# Revit family: TESK_Насос вертикальный_SVM(T)-200
name_source: partatom
category: Оборудование
units: mm (PartAtom-declared; Revit-internal decimal feet)

## family parameters
Всегда вертикально = Да
Классификация = Насос
На основе рабочей плоскости = Нет
Общий = Нет
При загрузке вырезать с полостями = Нет
Размер круглого соединителя = Использовать диаметр
Тип детали = Вставляется
Точка расчета площади = Нет

## types (34) — shared parameters
ADSK_Версия Revit = 2019
ADSK_Версия семейства = 1.0
ADSK_Диаметр условный = 150 мм
ADSK_Единица измерения = шт.
ADSK_Завод-изготовитель = TESK
ADSK_Классификация нагрузок = Прочее
ADSK_Количество = 1
ADSK_Количество фаз = 3
ADSK_Количество фаз числовое = 3
ADSK_Коэффициент мощности = 1
ADSK_Наименование краткое = Вертикальный многоступенчатый центробежный насос
ADSK_Напряжение = 400 В
URL = www.teskpump.ru
Материал_1 = TESK_Черный_Условный
Материал_2 = TESK_Нержавеющая сталь
Материал_КорпусДвигателя = TESK_Черный_Ребра_Условный
Таблица_Поиска = TESK_SVM(T)-200
УГО_Длина = 490 мм
Фланец_Толщина = 30 мм

## per-type parameters (varying)
| type | ADSK_Код изделия | ADSK_Масса | ADSK_Масса_Текст | ADSK_Наименование | ADSK_Номинальная мощность | ADSK_Полная мощность | D_Башня | Высота_Башня | Высота_Корпуса | Двигатель_Высота | Двигатель_ОтступКоробки | Двигатель_Ширина | Материал_КорпусУлитка | Напор максимальный | Толщина_ФланцаДвигателя |
| SVM 200-1-B 18.5kW 3x380V 50Hz IE3 | 77200-10-20003380NSSF | 311 | 311 | Вертикальный многоступенчатый центробежный насос SVM, DN150, PN25-40, Hmax=25.5м (3x380V 50Hz IE3) | 19 кВт | 19 кВ·А | 263 мм | 320 мм | 907 мм | 610 мм | 260 мм | 350 мм | TESK_Нержавеющая сталь | 25.5 | 18 мм |
| SVM 200-1-A 22kW 3x380V 50Hz IE3 | 77200-10-10003380NSSF | 347 | 347 | Вертикальный многоступенчатый центробежный насос SVM, DN150, PN25-40, Hmax=29м (3x380V 50Hz IE3) | 22 кВт | 22 кВ·А | 270 мм | 320 мм | 907 мм | 645 мм | 285 мм | 360 мм | TESK_Нержавеющая сталь | 29 | 19 мм |
| SVM 200-1 30kW 3x380V 50Hz IE3 | 77200-100003380NSSF | 403 | 403 | Вертикальный многоступенчатый центробежный насос SVM, DN150, PN25-40, Hmax=38.5м (3x380V 50Hz IE3) | 30 кВт | 30 кВ·А | 300 мм | 320 мм | 907 мм | 705 мм | 310 мм | 400 мм | TESK_Нержавеющая сталь | 38.5 | 21 мм |
| SVM 200-2-2B 37kW 3x380V 50Hz IE3 | 77200-20-220003380NSSF | 447 | 447 | Вертикальный многоступенчатый центробежный насос SVM, DN150, PN25-40, Hmax=53м (3x380V 50Hz IE3) | 37 кВт | 37 кВ·А | 300 мм | 360 мм | 1101 мм | 705 мм | 310 мм | 400 мм | TESK_Нержавеющая сталь | 53 | 21 мм |
| SVM 200-2-A 45kW 3x380V 50Hz IE3 | 77200-20-210003380NSSF | 504 | 504 | Вертикальный многоступенчатый центробежный насос SVM, DN150, PN25-40, Hmax=59.5м (3x380V 50Hz IE3) | 45 кВт | 45 кВ·А | 345 мм | 360 мм | 1101 мм | 740 мм | 340 мм | 460 мм | TESK_Нержавеющая сталь | 59.5 | 22 мм |
| SVM 200-2-A 55kW 3x380V 50Hz IE3 | 77200-20-10003380NSSF | 595 | 595 | Вертикальный многоступенчатый центробежный насос SVM, DN150, PN25-40, Hmax=69м (3x380V 50Hz IE3) | 55 кВт | 55 кВ·А | 413 мм | 380 мм | 1131 мм | 810 мм | 370 мм | 550 мм | TESK_Нержавеющая сталь | 69 | 24 мм |
| SVM 200-2 55kW 3x380V 50Hz IE3 | 77200-200003380NSSF | 595 | 595 | Вертикальный многоступенчатый центробежный насос SVM, DN150, PN25-40, Hmax=78.5м (3x380V 50Hz IE3) | 55 кВт | 55 кВ·А | 413 мм | 380 мм | 1131 мм | 810 мм | 370 мм | 550 мм | TESK_Нержавеющая сталь | 78.5 | 24 мм |
| SVM 200-3-2B 75kW 3x380V 50Hz IE3 | 77200-30-220003380NSSF | 748 | 748 | Вертикальный многоступенчатый центробежный насос SVM, DN150, PN25-40, Hmax=91.5м (3x380V 50Hz IE3) | 75 кВт | 75 кВ·А | 435 мм | 420 мм | 1325 мм | 870 мм | 410 мм | 580 мм | TESK_Нержавеющая сталь | 91.5 | 26 мм |
| SVM 200-3-A-B 75kW 3x380V 50Hz IE3 | 77200-30-1-20003380NSSF | 748 | 748 | Вертикальный многоступенчатый центробежный насос SVM, DN150, PN25-40, Hmax=95м (3x380V 50Hz IE3) | 75 кВт | 75 кВ·А | 435 мм | 420 мм | 1325 мм | 870 мм | 410 мм | 580 мм | TESK_Нержавеющая сталь | 95 | 26 мм |
| SVM 200-3-2A 75kW 3x380V 50Hz IE3 | 77200-30-210003380NSSF | 748 | 748 | Вертикальный многоступенчатый центробежный насос SVM, DN150, PN25-40, Hmax=99.5м (3x380V 50Hz IE3) | 75 кВт | 75 кВ·А | 435 мм | 420 мм | 1325 мм | 870 мм | 410 мм | 580 мм | TESK_Нержавеющая сталь | 99.5 | 26 мм |
| SVM 200-3-B 75kW 3x380V 50Hz IE3 | 77200-30-20003380NSSF | 748 | 748 | Вертикальный многоступенчатый центробежный насос SVM, DN150, PN25-40, Hmax=104.5м (3x380V 50Hz IE3) | 75 кВт | 75 кВ·А | 435 мм | 420 мм | 1325 мм | 870 мм | 410 мм | 580 мм | TESK_Нержавеющая сталь | 104.5 | 26 мм |
| SVM 200-3-A 75kW 3x380V 50Hz IE3 | 77200-30-10003380NSSF | 748 | 748 | Вертикальный многоступенчатый центробежный насос SVM, DN150, PN25-40, Hmax=108м (3x380V 50Hz IE3) | 75 кВт | 75 кВ·А | 435 мм | 420 мм | 1325 мм | 870 мм | 410 мм | 580 мм | TESK_Нержавеющая сталь | 108 | 26 мм |
| SVM 200-3 90kW 3x380V 50Hz IE3 | 77200-300003380NSSF | 816 | 816 | Вертикальный многоступенчатый центробежный насос SVM, DN150, PN25-40, Hmax=117.5м (3x380V 50Hz IE3) | 90 кВт | 90 кВ·А | 435 мм | 420 мм | 1325 мм | 920 мм | 410 мм | 580 мм | TESK_Нержавеющая сталь | 117.5 | 28 мм |
| SVM 200-4-2B 90kW 3x380V 50Hz IE3 | 77200-40-220003380NSSF | 830 | 830 | Вертикальный многоступенчатый центробежный насос SVM, DN150, PN25-40, Hmax=131.5м (3x380V 50Hz IE3) | 90 кВт | 90 кВ·А | 435 мм | 500 мм | 1519 мм | 920 мм | 410 мм | 580 мм | TESK_Нержавеющая сталь | 131.5 | 28 мм |
| SVM 200-4-2A 110kW 3x380V 50Hz IE3 | 77200-40-210003380NSSF | 1180 | 1180 | Вертикальный многоступенчатый центробежный насос SVM, DN150, PN25-40, Hmax=138.5м (3x380V 50Hz IE3) | 110 кВт | 110 кВ·А | 495 мм | 500 мм | 1519 мм | 1060 мм | 550 мм | 660 мм | TESK_Нержавеющая сталь | 138.5 | 32 мм |
| SVM 200-4-A 110kW 3x380V 50Hz IE3 | 77200-40-10003380NSSF | 1180 | 1180 | Вертикальный многоступенчатый центробежный насос SVM, DN150, PN25-40, Hmax=148м (3x380V 50Hz IE3) | 110 кВт | 110 кВ·А | 495 мм | 500 мм | 1519 мм | 1060 мм | 550 мм | 660 мм | TESK_Нержавеющая сталь | 148 | 32 мм |
| SVM 200-4 110kW 3x380V 50Hz IE3 | 77200-400003380NSSF | 1180 | 1180 | Вертикальный многоступенчатый центробежный насос SVM, DN150, PN25-40, Hmax=157.5м (3x380V 50Hz IE3) | 110 кВт | 110 кВ·А | 495 мм | 500 мм | 1519 мм | 1060 мм | 550 мм | 660 мм | TESK_Нержавеющая сталь | 157.5 | 32 мм |
| SVMT 200-1-B 18.5kW 3x380V 50Hz IE3 | 77200-10-20003380N | 311 | 311 | Вертикальный многоступенчатый центробежный насос SVMT, DN150, PN25-40, Hmax=25.5м (3x380V 50Hz IE3) | 19 кВт | 19 кВ·А | 263 мм | 320 мм | 907 мм | 610 мм | 260 мм | 350 мм | TESK_Черный_Условный | 25.5 | 18 мм |
| SVMT 200-1-A 22kW 3x380V 50Hz IE3 | 77200-10-10003380N | 347 | 347 | Вертикальный многоступенчатый центробежный насос SVMT, DN150, PN25-40, Hmax=29м (3x380V 50Hz IE3) | 22 кВт | 22 кВ·А | 270 мм | 320 мм | 907 мм | 645 мм | 285 мм | 360 мм | TESK_Черный_Условный | 29 | 19 мм |
| SVMT 200-1 30kW 3x380V 50Hz IE3 | 77200-100003380N | 403 | 403 | Вертикальный многоступенчатый центробежный насос SVMT, DN150, PN25-40, Hmax=38.5м (3x380V 50Hz IE3) | 30 кВт | 30 кВ·А | 300 мм | 320 мм | 907 мм | 705 мм | 310 мм | 400 мм | TESK_Черный_Условный | 38.5 | 21 мм |
| SVMT 200-2-2B 37kW 3x380V 50Hz IE3 | 77200-20-220003380N | 447 | 447 | Вертикальный многоступенчатый центробежный насос SVMT, DN150, PN25-40, Hmax=53м (3x380V 50Hz IE3) | 37 кВт | 37 кВ·А | 300 мм | 360 мм | 1101 мм | 705 мм | 310 мм | 400 мм | TESK_Черный_Условный | 53 | 21 мм |
| SVMT 200-2-A 45kW 3x380V 50Hz IE3 | 77200-20-210003380N | 504 | 504 | Вертикальный многоступенчатый центробежный насос SVMT, DN150, PN25-40, Hmax=59.5м (3x380V 50Hz IE3) | 45 кВт | 45 кВ·А | 345 мм | 360 мм | 1101 мм | 740 мм | 340 мм | 460 мм | TESK_Черный_Условный | 59.5 | 22 мм |
| SVMT 200-2-A 55kW 3x380V 50Hz IE3 | 77200-20-10003380N | 595 | 595 | Вертикальный многоступенчатый центробежный насос SVMT, DN150, PN25-40, Hmax=69м (3x380V 50Hz IE3) | 55 кВт | 55 кВ·А | 413 мм | 380 мм | 1131 мм | 810 мм | 370 мм | 550 мм | TESK_Черный_Условный | 69 | 24 мм |
| SVMT 200-2 55kW 3x380V 50Hz IE3 | 77200-200003380N | 595 | 595 | Вертикальный многоступенчатый центробежный насос SVMT, DN150, PN25-40, Hmax=78.5м (3x380V 50Hz IE3) | 55 кВт | 55 кВ·А | 413 мм | 380 мм | 1131 мм | 810 мм | 370 мм | 550 мм | TESK_Черный_Условный | 78.5 | 24 мм |
| SVMT 200-3-2B 75kW 3x380V 50Hz IE3 | 77200-30-220003380N | 748 | 748 | Вертикальный многоступенчатый центробежный насос SVMT, DN150, PN25-40, Hmax=91.5м (3x380V 50Hz IE3) | 75 кВт | 75 кВ·А | 435 мм | 420 мм | 1325 мм | 870 мм | 410 мм | 580 мм | TESK_Черный_Условный | 91.5 | 26 мм |
| SVMT 200-3-A-B 75kW 3x380V 50Hz IE3 | 77200-30-1-20003380N | 748 | 748 | Вертикальный многоступенчатый центробежный насос SVMT, DN150, PN25-40, Hmax=95м (3x380V 50Hz IE3) | 75 кВт | 75 кВ·А | 435 мм | 420 мм | 1325 мм | 870 мм | 410 мм | 580 мм | TESK_Черный_Условный | 95 | 26 мм |
| SVMT 200-3-2A 75kW 3x380V 50Hz IE3 | 77200-30-210003380N | 748 | 748 | Вертикальный многоступенчатый центробежный насос SVMT, DN150, PN25-40, Hmax=99.5м (3x380V 50Hz IE3) | 75 кВт | 75 кВ·А | 435 мм | 420 мм | 1325 мм | 870 мм | 410 мм | 580 мм | TESK_Черный_Условный | 99.5 | 26 мм |
| SVMT 200-3-B 75kW 3x380V 50Hz IE3 | 77200-30-20003380N | 748 | 748 | Вертикальный многоступенчатый центробежный насос SVMT, DN150, PN25-40, Hmax=104.5м (3x380V 50Hz IE3) | 75 кВт | 75 кВ·А | 435 мм | 420 мм | 1325 мм | 870 мм | 410 мм | 580 мм | TESK_Черный_Условный | 104.5 | 26 мм |
| SVMT 200-3-A 75kW 3x380V 50Hz IE3 | 77200-30-10003380N | 748 | 748 | Вертикальный многоступенчатый центробежный насос SVMT, DN150, PN25-40, Hmax=108м (3x380V 50Hz IE3) | 75 кВт | 75 кВ·А | 435 мм | 420 мм | 1325 мм | 870 мм | 410 мм | 580 мм | TESK_Черный_Условный | 108 | 26 мм |
| SVMT 200-3 90kW 3x380V 50Hz IE3 | 77200-300003380N | 816 | 816 | Вертикальный многоступенчатый центробежный насос SVMT, DN150, PN25-40, Hmax=117.5м (3x380V 50Hz IE3) | 90 кВт | 90 кВ·А | 435 мм | 420 мм | 1325 мм | 920 мм | 410 мм | 580 мм | TESK_Черный_Условный | 117.5 | 28 мм |
| SVMT 200-4-2B 90kW 3x380V 50Hz IE3 | 77200-40-220003380N | 830 | 830 | Вертикальный многоступенчатый центробежный насос SVMT, DN150, PN25-40, Hmax=131.5м (3x380V 50Hz IE3) | 90 кВт | 90 кВ·А | 435 мм | 500 мм | 1519 мм | 920 мм | 410 мм | 580 мм | TESK_Черный_Условный | 131.5 | 28 мм |
| SVMT 200-4-2A 110kW 3x380V 50Hz IE3 | 77200-40-210003380N | 1180 | 1180 | Вертикальный многоступенчатый центробежный насос SVMT, DN150, PN25-40, Hmax=138.5м (3x380V 50Hz IE3) | 110 кВт | 110 кВ·А | 495 мм | 500 мм | 1519 мм | 1060 мм | 550 мм | 660 мм | TESK_Черный_Условный | 138.5 | 32 мм |
| SVMT 200-4-A 110kW 3x380V 50Hz IE3 | 77200-40-10003380N | 1180 | 1180 | Вертикальный многоступенчатый центробежный насос SVMT, DN150, PN25-40, Hmax=148м (3x380V 50Hz IE3) | 110 кВт | 110 кВ·А | 495 мм | 500 мм | 1519 мм | 1060 мм | 550 мм | 660 мм | TESK_Черный_Условный | 148 | 32 мм |
| SVMT 200-4 110kW 3x380V 50Hz IE3 | 77200-400003380N | 1180 | 1180 | Вертикальный многоступенчатый центробежный насос SVMT, DN150, PN25-40, Hmax=157.5м (3x380V 50Hz IE3) | 110 кВт | 110 кВ·А | 495 мм | 500 мм | 1519 мм | 1060 мм | 550 мм | 660 мм | TESK_Черный_Условный | 157.5 | 32 мм |

note: column(s) folded — value = type name in every type: ADSK_Марка
